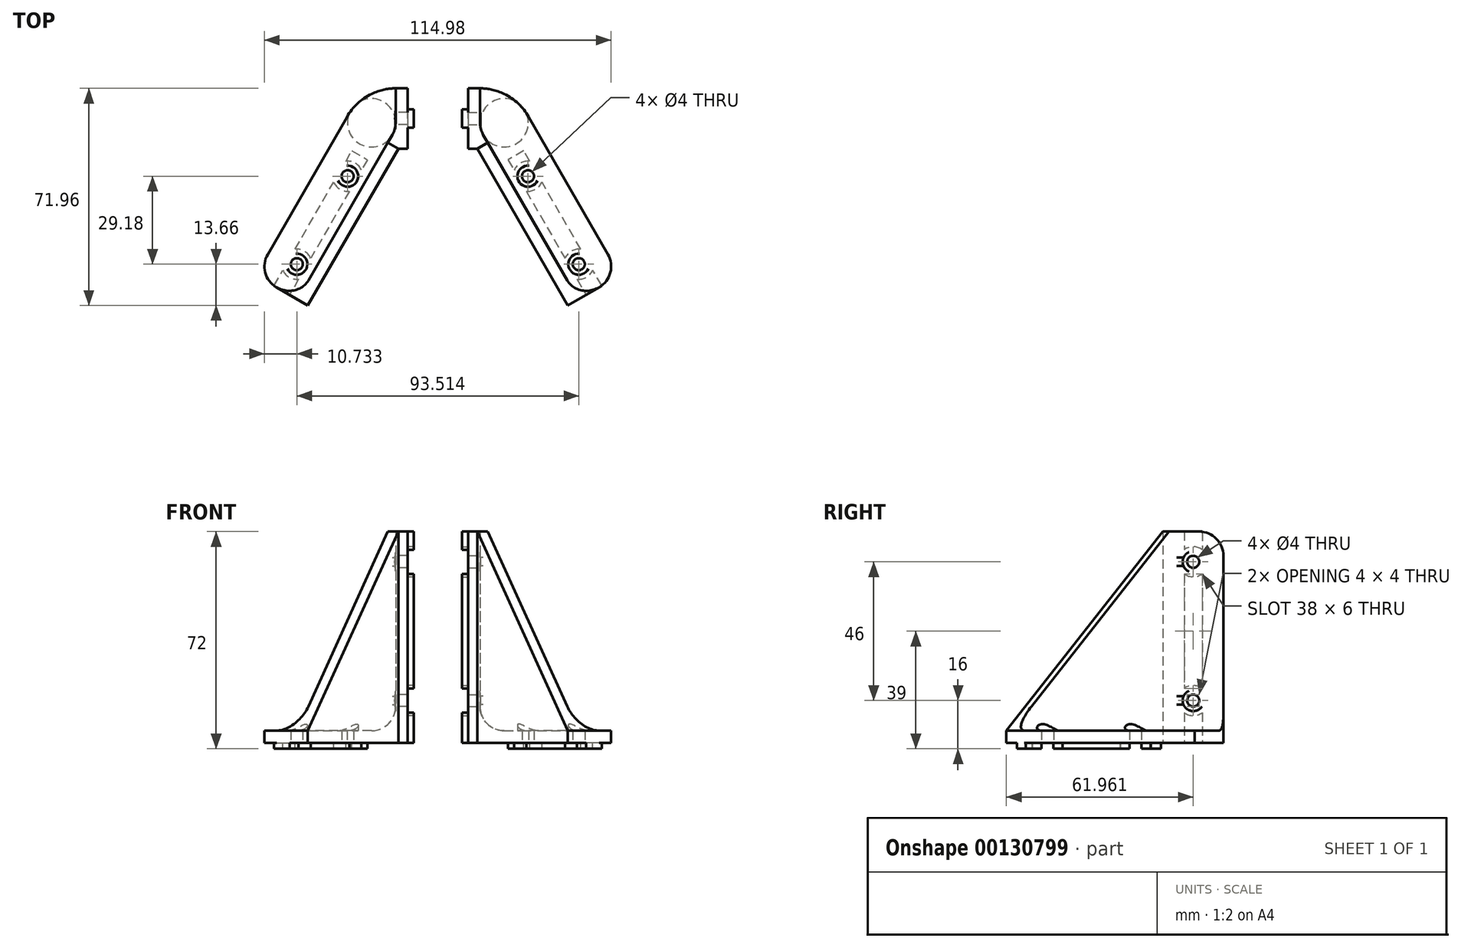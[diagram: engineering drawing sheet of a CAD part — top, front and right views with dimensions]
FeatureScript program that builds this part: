
annotation { "Feature Type Name" : "Feature", "Feature Type Description" : "" }
export const myFeature = defineFeature(function(context is Context, id is Id, definition is map)
    precondition{}
    {
        {
            var Q0;
            Q0=qCreatedBy(makeId("Top.planeOp"),FACE);
            var sketch = newSketch(context, id + "F0", { "sketchPlane" : qUnion([Q0])});
            skCircle(sketch, "E0.cCircle", {"center": v(0, 0) * mm, "radius": 185.13 * mm, "construction": true});
            skLineSegment(sketch, "E0.0", {"start": v(320.65, -185.13) * mm, "end": v(-320.65, -185.13) * mm});
            skLineSegment(sketch, "E0.1", {"start": v(-320.65, -185.13) * mm, "end": v(0, 370.26) * mm});
            skLineSegment(sketch, "E0.2", {"start": v(0, 370.26) * mm, "end": v(320.65, -185.13) * mm});
            skPoint(sketch, "E0.0.midPoint", {"position": v(0, -185.13) * mm});
            skCircle(sketch, "E1.cCircle", {"center": v(0, 0) * mm, "radius": 165.13 * mm, "construction": true});
            skLineSegment(sketch, "E1.0", {"start": v(286, -165.13) * mm, "end": v(-286, -165.13) * mm});
            skLineSegment(sketch, "E1.1", {"start": v(-286, -165.13) * mm, "end": v(0, 330.26) * mm});
            skLineSegment(sketch, "E1.2", {"start": v(0, 330.26) * mm, "end": v(286, -165.13) * mm});
            skPoint(sketch, "E1.0.midPoint", {"position": v(0, -165.13) * mm});
            skLineSegment(sketch, "E2", {"start": v(16.25, 302.1) * mm, "end": v(33.57, 312.1) * mm});
            skLineSegment(sketch, "E3", {"start": v(136.25, 94.26) * mm, "end": v(153.57, 104.26) * mm});
            skLineSegment(sketch, "E4", {"start": v(-16.25, 302.1) * mm, "end": v(-33.57, 312.1) * mm});
            skLineSegment(sketch, "E5", {"start": v(-136.25, 94.26) * mm, "end": v(-153.57, 104.26) * mm});
            skLineSegment(sketch, "E6.bottom", {"start": v(-10, 327.57) * mm, "end": v(10, 327.57) * mm});
            skLineSegment(sketch, "E6.top", {"start": v(-10, 307.57) * mm, "end": v(10, 307.57) * mm});
            skLineSegment(sketch, "E6.left", {"start": v(-10, 327.57) * mm, "end": v(-10, 307.57) * mm});
            skLineSegment(sketch, "E6.right", {"start": v(10, 327.57) * mm, "end": v(10, 307.57) * mm});
            skLineSegment(sketch, "E7", {"start": v(0, 456.85) * mm, "end": v(0, -199.59) * mm});
            skCircle(sketch, "E8", {"center": v(0, 298.8) * mm, "radius": 35.77 * mm});
            skLineSegment(sketch, "E9", {"start": v(0, 327.57) * mm, "end": v(0, 334.57) * mm});
            skPoint(sketch, "E10", {"position": v(0, 307.57) * mm});
            skSolve(sketch);
        }
        {
            var Q0;
            Q0=qCreatedBy(makeId("Top.planeOp"),FACE);
            var sketch = newSketch(context, id + "F1", { "sketchPlane" : qUnion([Q0])});
            skLineSegment(sketch, "E11.bottom", {"start": v(-14, 327.57) * mm, "end": v(-10, 327.57) * mm});
            skLineSegment(sketch, "E11.top", {"start": v(-14, 307.57) * mm, "end": v(-10, 307.57) * mm});
            skLineSegment(sketch, "E11.left", {"start": v(-14, 327.57) * mm, "end": v(-14, 307.57) * mm});
            skLineSegment(sketch, "E11.right", {"start": v(-10, 327.57) * mm, "end": v(-10, 307.57) * mm});
            skLineSegment(sketch, "E12", {"start": v(-43.1, 255.6) * mm, "end": v(-13.1, 307.57) * mm});
            skLineSegment(sketch, "E13", {"start": v(-14, 314) * mm, "end": v(-46.56, 257.6) * mm});
            skLineSegment(sketch, "E14", {"start": v(-43.1, 255.6) * mm, "end": v(-60.42, 265.6) * mm});
            skLineSegment(sketch, "E15", {"start": v(-60.42, 265.6) * mm, "end": v(-30.12, 318.09) * mm});
            skArc(sketch, "E16", {"start": v(-14, 327.57) * mm, "mid": v(-23.35, 325.02) * mm, "end": v(-30.12, 318.09) * mm});
            skLineSegment(sketch, "E17", {"start": v(-51.76, 260.6) * mm, "end": v(-25.68, 305.77) * mm});
            skCircle(sketch, "E18", {"center": v(-46.76, 269.27) * mm, "radius": 2 * mm});
            skCircle(sketch, "E19", {"center": v(-29.91, 298.45) * mm, "radius": 2 * mm});
            skSolve(sketch);
        }
        {
            var Q0;
            Q0 = qSketchRegion(id + "F1", true);
            extrude(context, id + "F2", {"entities" : qUnion([Q0]), "depth" : 4 * mm});
        }
        {
            var Q0;
            Q0=qCreatedBy(makeId("Top.planeOp"),FACE);
            var sketch = newSketch(context, id + "F3", { "sketchPlane" : qUnion([Q0])});
            skLineSegment(sketch, "E20", {"start": v(-43.1, 255.6) * mm, "end": v(-46.56, 257.6) * mm});
            skLineSegment(sketch, "E21", {"start": v(-46.56, 257.6) * mm, "end": v(-14, 314) * mm});
            skLineSegment(sketch, "E22", {"start": v(-14, 314) * mm, "end": v(-14, 327.57) * mm});
            skLineSegment(sketch, "E23", {"start": v(-14, 327.57) * mm, "end": v(-10, 327.57) * mm});
            skLineSegment(sketch, "E24", {"start": v(-10, 327.57) * mm, "end": v(-10, 307.57) * mm});
            skLineSegment(sketch, "E25", {"start": v(-10, 307.57) * mm, "end": v(-13.1, 307.57) * mm});
            skLineSegment(sketch, "E26", {"start": v(-13.1, 307.57) * mm, "end": v(-43.1, 255.6) * mm});
            skSolve(sketch);
        }
        {
            var Q0;
            Q0 = qSketchRegion(id + "F3", true);
            extrude(context, id + "F4", {"entities" : qUnion([Q0]), "operationType" : NewBodyOperationType.ADD, "depth" : 70 * mm});
        }
        {
            var Q0;
            Q0=makeQuery(id+"F4.boolean.opBoolean","MERGE",FACE,{"derivedFrom":[makeQuery(id+"F2.opExtrude","SWEPT_FACE",FACE,{"disambiguationData":[OSD([sQuery(id+"F1.wireOp",EDGE,"E12")])]}),makeQuery(id+"F4.opExtrude","SWEPT_FACE",FACE,{"disambiguationData":[OSD([sQuery(id+"F3.wireOp",EDGE,"E26")])]})]});
            var sketch = newSketch(context, id + "F5", { "sketchPlane" : qUnion([Q0])});
            skLineSegment(sketch, "E27", {"start": v(259.82, 70) * mm, "end": v(199.82, 4) * mm});
            skLineSegment(sketch, "E28", {"start": v(199.82, 4) * mm, "end": v(199.82, 70) * mm});
            skLineSegment(sketch, "E29", {"start": v(199.82, 70) * mm, "end": v(259.82, 70) * mm});
            skSolve(sketch);
        }
        {
            var Q0;
            Q0=makeQuery(id+"F5.imprint","IMPRINT",FACE,{"disambiguationData":[TD([[makeQuery(id+"F5.imprint","IMPRINT",EDGE,{"derivedFrom":sQuery(id+"F5.wireOp",EDGE,"E27")}),-1.0]])]});
            extrude(context, id + "F6", {"entities" : qUnion([Q0]), "operationType" : NewBodyOperationType.REMOVE, "endBound" : BoundingType.THROUGH_ALL, "oppositeDirection" : true, "depth" : 25 * mm});
        }
        {
            var Q0;
            Q0=makeQuery(id+"F4.opExtrude","SWEPT_FACE",FACE,{"disambiguationData":[OSD([sQuery(id+"F3.wireOp",EDGE,"E22")])]});
            var sketch = newSketch(context, id + "F7", { "sketchPlane" : qUnion([Q0])});
            skCircle(sketch, "E30", {"center": v(-317.57, 60) * mm, "radius": 2 * mm});
            skCircle(sketch, "E31", {"center": v(-317.57, 14) * mm, "radius": 2 * mm});
            skSolve(sketch);
        }
        {
            var Q0;
            Q0=makeQuery(id+"F7.imprint","IMPRINT",FACE,{"disambiguationData":[TD([[makeQuery(id+"F7.imprint","IMPRINT",EDGE,{"derivedFrom":sQuery(id+"F7.wireOp",EDGE,"E30")}),1.0]])]});
            var sketch = newSketch(context, id + "F8", { "sketchPlane" : qUnion([Q0])});
            skSolve(sketch);
        }
        {
            var Q0;
            Q0 = qSketchRegion(id + "F8", true);
            var Q1;
            Q1=makeQuery(id+"F7.imprint","IMPRINT",FACE,{"disambiguationData":[TD([[makeQuery(id+"F7.imprint","IMPRINT",EDGE,{"derivedFrom":sQuery(id+"F7.wireOp",EDGE,"E31")}),1.0]])]});
            var Q2;
            Q2=makeQuery(id+"F7.imprint","IMPRINT",FACE,{"disambiguationData":[TD([[makeQuery(id+"F7.imprint","IMPRINT",EDGE,{"derivedFrom":sQuery(id+"F7.wireOp",EDGE,"E30")}),1.0]])]});
            extrude(context, id + "F9", {"entities" : qUnion([Q0, Q1, Q2]), "operationType" : NewBodyOperationType.REMOVE, "endBound" : BoundingType.THROUGH_ALL, "oppositeDirection" : true, "depth" : 25 * mm});
        }
        {
            var Q0;
            Q0=makeQuery(id+"F4.boolean.opBoolean","INTERSECT",EDGE,{"derivedFrom":[makeQuery(id+"F2.opExtrude","CAP_FACE",FACE,{"disambiguationData":[OSD([sQuery(id+"F1.wireOp",EDGE,"E11.bottom"),sQuery(id+"F1.wireOp",EDGE,"E11.top"),sQuery(id+"F1.wireOp",EDGE,"E11.right"),sQuery(id+"F1.wireOp",EDGE,"E12"),sQuery(id+"F1.wireOp",EDGE,"E14"),sQuery(id+"F1.wireOp",EDGE,"E15"),sQuery(id+"F1.wireOp",EDGE,"E16"),sQuery(id+"F1.wireOp",EDGE,"E18"),sQuery(id+"F1.wireOp",EDGE,"E19")])],"isStart":false}),makeQuery(id+"F4.opExtrude","SWEPT_FACE",FACE,{"disambiguationData":[OSD([sQuery(id+"F3.wireOp",EDGE,"E21")])]})]});
            var Q1;
            Q1=makeQuery(id+"F2.opExtrude","SWEPT_EDGE",EDGE,{"disambiguationData":[OSD([sQuery(id+"F1.wireOp",EDGE,"E14"),sQuery(id+"F1.wireOp",EDGE,"E15")])]});
            var Q2;
            Q2=makeQuery(id+"F4.opExtrude","CAP_EDGE",EDGE,{"disambiguationData":[OSD([sQuery(id+"F3.wireOp",EDGE,"E23")])],"isStart":false});
            var Q3;
            Q3=makeQuery(id+"F4.opExtrude","SWEPT_EDGE",EDGE,{"disambiguationData":[OSD([sQuery(id+"F3.wireOp",EDGE,"E21"),sQuery(id+"F3.wireOp",EDGE,"E22")])]});
            var Q4;
            Q4=makeQuery(id+"F4.boolean.opBoolean","INTERSECT",EDGE,{"derivedFrom":[makeQuery(id+"F2.opExtrude","CAP_FACE",FACE,{"disambiguationData":[OSD([sQuery(id+"F1.wireOp",EDGE,"E11.bottom"),sQuery(id+"F1.wireOp",EDGE,"E11.top"),sQuery(id+"F1.wireOp",EDGE,"E11.right"),sQuery(id+"F1.wireOp",EDGE,"E12"),sQuery(id+"F1.wireOp",EDGE,"E14"),sQuery(id+"F1.wireOp",EDGE,"E15"),sQuery(id+"F1.wireOp",EDGE,"E16"),sQuery(id+"F1.wireOp",EDGE,"E18"),sQuery(id+"F1.wireOp",EDGE,"E19")])],"isStart":false}),makeQuery(id+"F4.opExtrude","SWEPT_FACE",FACE,{"disambiguationData":[OSD([sQuery(id+"F3.wireOp",EDGE,"E22")])]})]});
            fillet(context, id + "F10", {"entities" : qUnion([Q0, Q1, Q2, Q3, Q4]), "radius" : 8 * mm, "tangentPropagation" : true, "allowEdgeOverflow" : false});
        }
        {
            var Q0;
            Q0=makeQuery(id+"F2.opExtrude","CAP_FACE",FACE,{"disambiguationData":[OSD([sQuery(id+"F1.wireOp",EDGE,"E11.bottom"),sQuery(id+"F1.wireOp",EDGE,"E11.top"),sQuery(id+"F1.wireOp",EDGE,"E11.right"),sQuery(id+"F1.wireOp",EDGE,"E12"),sQuery(id+"F1.wireOp",EDGE,"E14"),sQuery(id+"F1.wireOp",EDGE,"E15"),sQuery(id+"F1.wireOp",EDGE,"E16"),sQuery(id+"F1.wireOp",EDGE,"E18"),sQuery(id+"F1.wireOp",EDGE,"E19")])],"isStart":false});
            var sketch = newSketch(context, id + "F11", { "sketchPlane" : qUnion([Q0])});
            skCircle(sketch, "E32", {"center": v(-46.76, 269.27) * mm, "radius": 3.5 * mm});
            skCircle(sketch, "E33", {"center": v(-29.91, 298.45) * mm, "radius": 3.5 * mm});
            skSolve(sketch);
        }
        {
            var Q0;
            Q0 = qSketchRegion(id + "F11", true);
            extrude(context, id + "F12", {"entities" : qUnion([Q0]), "operationType" : NewBodyOperationType.REMOVE, "endBound" : BoundingType.THROUGH_ALL, "depth" : 25 * mm});
        }
        {
            var Q0;
            Q0=makeQuery(id+"F4.opExtrude","SWEPT_FACE",FACE,{"disambiguationData":[OSD([sQuery(id+"F3.wireOp",EDGE,"E22")])]});
            var sketch = newSketch(context, id + "F13", { "sketchPlane" : qUnion([Q0])});
            skCircle(sketch, "E34", {"center": v(-317.57, 60) * mm, "radius": 3.5 * mm});
            skCircle(sketch, "E35", {"center": v(-317.57, 14) * mm, "radius": 3.5 * mm});
            skSolve(sketch);
        }
        {
            var Q0;
            Q0 = qSketchRegion(id + "F13", true);
            extrude(context, id + "F14", {"entities" : qUnion([Q0]), "operationType" : NewBodyOperationType.REMOVE, "endBound" : BoundingType.THROUGH_ALL, "depth" : 25 * mm});
        }
        {
            var Q0;
            Q0=makeQuery(id+"F4.boolean.opBoolean","MERGE",FACE,{"derivedFrom":[makeQuery(id+"F2.opExtrude","SWEPT_FACE",FACE,{"disambiguationData":[OSD([sQuery(id+"F1.wireOp",EDGE,"E11.right")])]}),makeQuery(id+"F4.opExtrude","SWEPT_FACE",FACE,{"disambiguationData":[OSD([sQuery(id+"F3.wireOp",EDGE,"E24")])]})]});
            var sketch = newSketch(context, id + "F15", { "sketchPlane" : qUnion([Q0])});
            skLineSegment(sketch, "E36.bottom", {"start": v(314.57, 70) * mm, "end": v(320.57, 70) * mm});
            skLineSegment(sketch, "E36.top", {"start": v(314.57, 0) * mm, "end": v(320.57, 0) * mm});
            skLineSegment(sketch, "E36.left", {"start": v(314.57, 70) * mm, "end": v(314.57, 64) * mm});
            skLineSegment(sketch, "E36.right", {"start": v(320.57, 70) * mm, "end": v(320.57, 64) * mm});
            skArc(sketch, "E37", {"start": v(320.57, 64) * mm, "mid": v(317.57, 65) * mm, "end": v(314.57, 64) * mm});
            skArc(sketch, "E38", {"start": v(320.57, 18) * mm, "mid": v(317.57, 19) * mm, "end": v(314.57, 18) * mm});
            skLineSegment(sketch, "E39.trimOffspring", {"start": v(314.57, 56) * mm, "end": v(314.57, 18) * mm});
            skLineSegment(sketch, "E40.trimOffspring", {"start": v(320.57, 56) * mm, "end": v(320.57, 18) * mm});
            skArc(sketch, "E41.trimOffspring", {"start": v(314.57, 56) * mm, "mid": v(317.57, 55) * mm, "end": v(320.57, 56) * mm});
            skLineSegment(sketch, "E42.trimOffspring", {"start": v(314.57, 10) * mm, "end": v(314.57, 0) * mm});
            skLineSegment(sketch, "E43.trimOffspring", {"start": v(320.57, 10) * mm, "end": v(320.57, 0) * mm});
            skArc(sketch, "E44.trimOffspring", {"start": v(314.57, 10) * mm, "mid": v(317.57, 9) * mm, "end": v(320.57, 10) * mm});
            skSolve(sketch);
        }
        {
            var Q0;
            Q0 = qSketchRegion(id + "F15", true);
            extrude(context, id + "F16", {"entities" : qUnion([Q0]), "operationType" : NewBodyOperationType.ADD, "depth" : 2 * mm});
        }
        {
            var Q0;
            {var subQ0=sQuery(id+"F0.wireOp",EDGE,"E5");Q0=makeQuery(id+"F0.imprint","IMPRINT",FACE,{"disambiguationData":[TD([[makeQuery(id+"F0.imprint","IMPRINT",EDGE,{"derivedFrom":subQ0}),-1.0]])]});}
            var sketch = newSketch(context, id + "F17", { "sketchPlane" : qUnion([Q0])});
            skLineSegment(sketch, "E45", {"start": v(-28.5, 306.88) * mm, "end": v(-23.31, 303.88) * mm});
            skLineSegment(sketch, "E46", {"start": v(-23.31, 303.88) * mm, "end": v(-25.31, 300.41) * mm});
            skLineSegment(sketch, "E47", {"start": v(-49.16, 259.1) * mm, "end": v(-54.36, 262.1) * mm});
            skLineSegment(sketch, "E48", {"start": v(-54.36, 262.1) * mm, "end": v(-51.36, 267.3) * mm});
            skArc(sketch, "E49", {"start": v(-51.36, 267.3) * mm, "mid": v(-49.26, 264.94) * mm, "end": v(-46.16, 264.3) * mm});
            skArc(sketch, "E50", {"start": v(-34.5, 296.49) * mm, "mid": v(-32.41, 294.12) * mm, "end": v(-29.31, 293.49) * mm});
            skLineSegment(sketch, "E51.trimOffspring", {"start": v(-47.36, 274.23) * mm, "end": v(-34.5, 296.49) * mm});
            skLineSegment(sketch, "E52.trimOffspring", {"start": v(-46.16, 264.3) * mm, "end": v(-49.16, 259.1) * mm});
            skLineSegment(sketch, "E53.trimOffspring", {"start": v(-30.5, 303.41) * mm, "end": v(-28.5, 306.88) * mm});
            skLineSegment(sketch, "E54.trimOffspring", {"start": v(-29.31, 293.49) * mm, "end": v(-42.16, 271.23) * mm});
            skArc(sketch, "E55.trimOffspring", {"start": v(-25.31, 300.41) * mm, "mid": v(-27.41, 302.78) * mm, "end": v(-30.5, 303.41) * mm});
            skArc(sketch, "E56.trimOffspring", {"start": v(-42.16, 271.23) * mm, "mid": v(-44.26, 273.6) * mm, "end": v(-47.36, 274.23) * mm});
            skSolve(sketch);
        }
        {
            var Q0;
            Q0 = qSketchRegion(id + "F17", true);
            extrude(context, id + "F18", {"entities" : qUnion([Q0]), "operationType" : NewBodyOperationType.ADD, "oppositeDirection" : true, "depth" : 2 * mm});
        }
        {
            var Q0;
            Q0=makeQuery(id+"F2.opExtrude","SWEPT_BODY",BODY,{"disambiguationData":[OSD([sQuery(id+"F1.wireOp",EDGE,"E11.bottom"),sQuery(id+"F1.wireOp",EDGE,"E11.top"),sQuery(id+"F1.wireOp",EDGE,"E11.right"),sQuery(id+"F1.wireOp",EDGE,"E12"),sQuery(id+"F1.wireOp",EDGE,"E14"),sQuery(id+"F1.wireOp",EDGE,"E15"),sQuery(id+"F1.wireOp",EDGE,"E16"),sQuery(id+"F1.wireOp",EDGE,"E18"),sQuery(id+"F1.wireOp",EDGE,"E19")])]});
            var Q1;
            Q1=qCreatedBy(makeId("Right.planeOp"),FACE);
            mirror(context, id + "F19", {"entities" : qUnion([Q0]), "mirrorPlane" : qUnion([Q1])});
        }
    });
